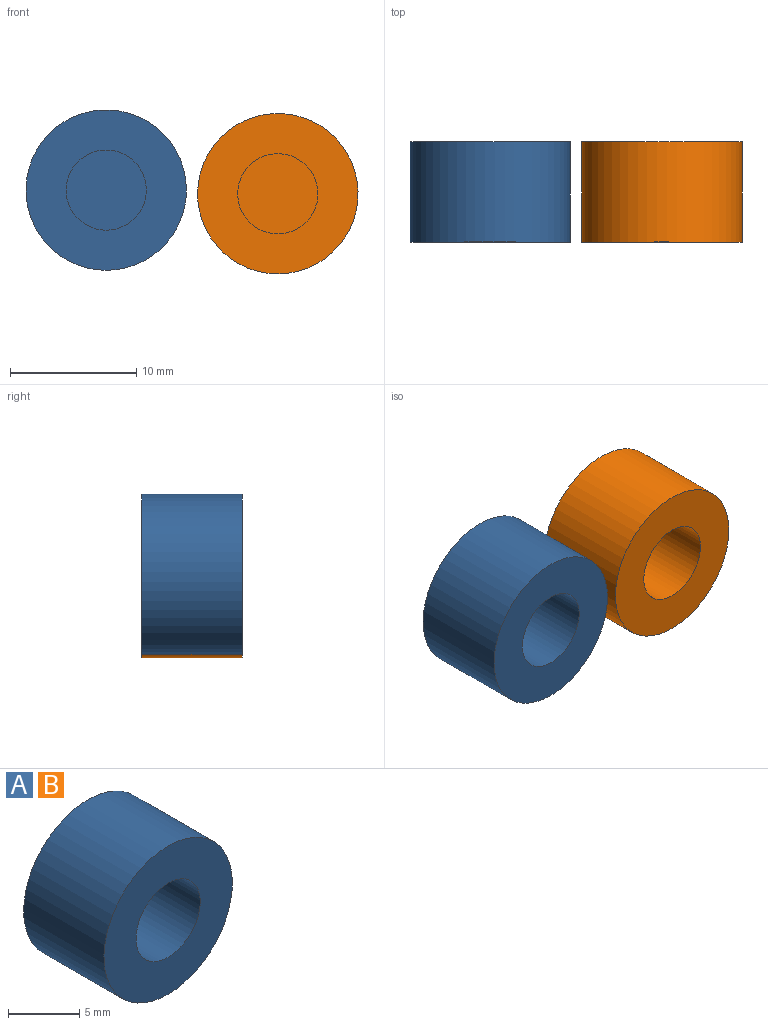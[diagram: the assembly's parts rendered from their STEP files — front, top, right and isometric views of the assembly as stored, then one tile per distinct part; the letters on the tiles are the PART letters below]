
ASSEMBLY  parts=2 mates=1
PART A: 5 faces, bbox 12.7x7.9x12.7 mm
  f0: cylinder r=6.35mm len=12.7mm, axis (0,1,0), area 316.7mm2, adj f1,f3
  f1: plane 12.7x12.7mm, normal (0,1,0), area 126.7mm2, adj f0
  f2: cylinder r=3.17mm len=6.35mm, axis (0,1,0), area 126.7mm2, adj f3,f4
  f3: plane 12.7x12.7mm, normal (0,-1,0), area 95mm2, adj f0,f2
  f4: plane 6.35x6.35mm, normal (0,-1,0), area 31.7mm2, adj f2
PART B: same geometry as A
PLACE A t=(-15.5,6.38,0.08)mm
PLACE B t=(-1.91,6.38,-0.21)mm
MATE planar B.f0 <-> A.f0  axis (0,-1,0) through (-1.91,-1.56,-0.21)mm
